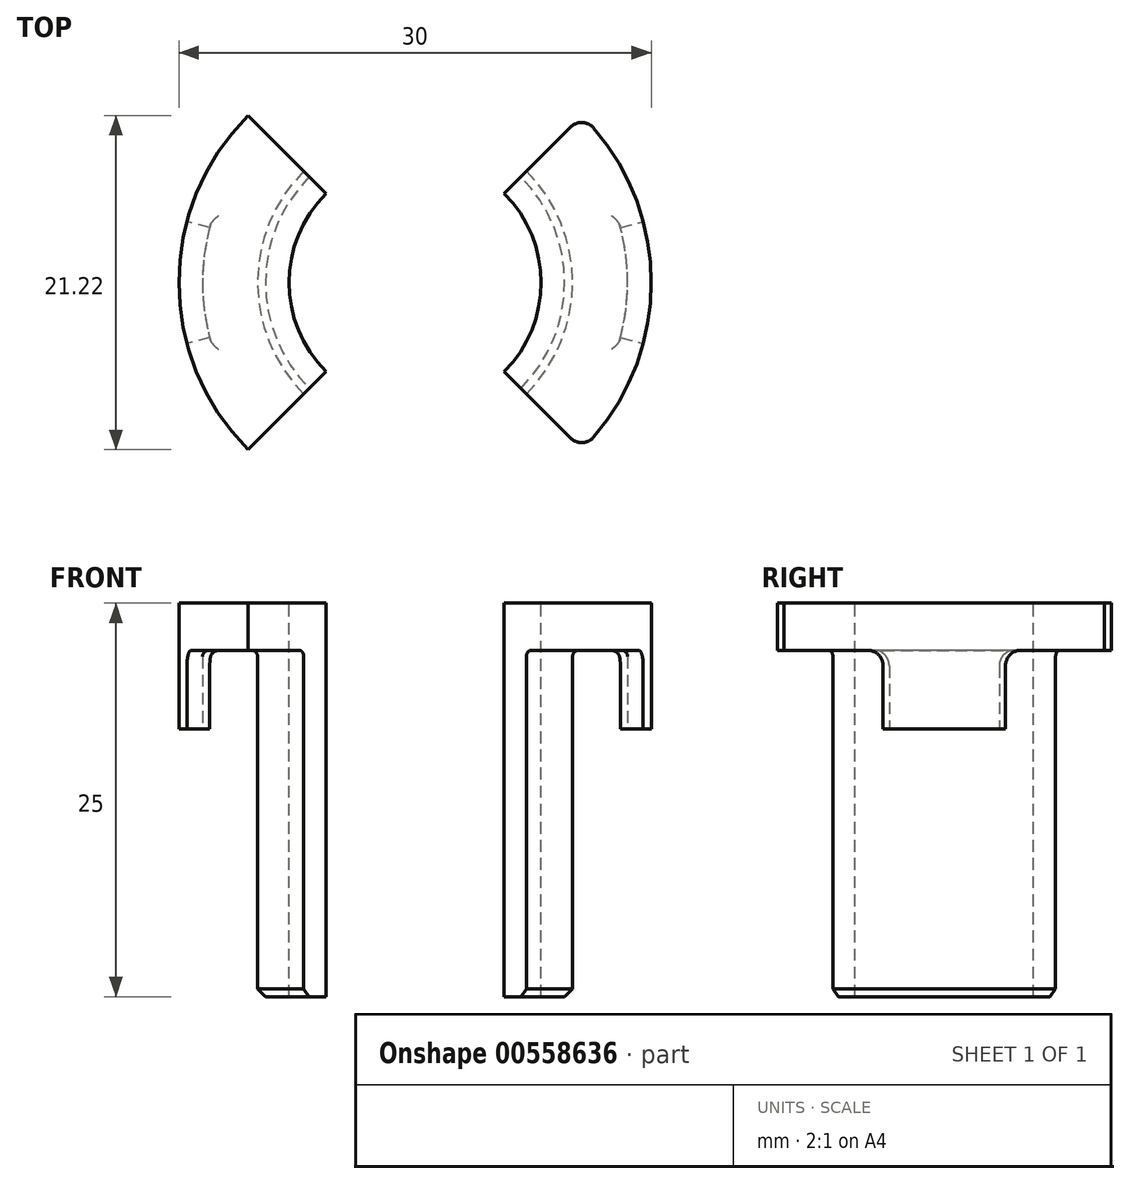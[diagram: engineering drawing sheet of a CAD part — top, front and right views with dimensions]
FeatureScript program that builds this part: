
annotation { "Feature Type Name" : "Feature", "Feature Type Description" : "" }
export const myFeature = defineFeature(function(context is Context, id is Id, definition is map)
    precondition{}
    {
        {
            var Q0;
            Q0=qCreatedBy(makeId("Top.planeOp"),FACE);
            var sketch = newSketch(context, id + "F0", { "sketchPlane" : qUnion([Q0])});
            skCircle(sketch, "E0", {"center": v(0, 0) * mm, "radius": 10 * mm});
            skCircle(sketch, "E1", {"center": v(0, 0) * mm, "radius": 8 * mm});
            skSolve(sketch);
        }
        {
            var Q0;
            Q0 = qSketchRegion(id + "F0", true);
            extrude(context, id + "F1", {"entities" : qUnion([Q0]), "oppositeDirection" : true, "depth" : 25 * mm, "offsetDistance" : 25 * mm});
        }
        {
            var Q0;
            Q0=qCreatedBy(makeId("Top.planeOp"),FACE);
            var sketch = newSketch(context, id + "F2", { "sketchPlane" : qUnion([Q0])});
            skCircle(sketch, "E2", {"center": v(0, 0) * mm, "radius": 15 * mm});
            skCircle(sketch, "E3.0", {"center": v(0, 0) * mm, "radius": 8 * mm});
            skSolve(sketch);
        }
        {
            var Q0;
            Q0 = qSketchRegion(id + "F2", true);
            extrude(context, id + "F3", {"entities" : qUnion([Q0]), "operationType" : NewBodyOperationType.ADD, "oppositeDirection" : true, "depth" : 8 * mm, "offsetDistance" : 25 * mm});
        }
        {
            var Q0;
            Q0=makeQuery(id+"F3.opExtrude","CAP_FACE",FACE,{"disambiguationData":[OSD([sQuery(id+"F2.wireOp",EDGE,"E2"),sQuery(id+"F2.wireOp",EDGE,"E3.0")])],"isStart":false});
            var sketch = newSketch(context, id + "F4", { "sketchPlane" : qUnion([Q0])});
            skCircle(sketch, "E4", {"center": v(0, 0) * mm, "radius": 13.5 * mm});
            skCircle(sketch, "E5.0", {"center": v(0, 0) * mm, "radius": 10 * mm});
            skSolve(sketch);
        }
        {
            var Q0;
            Q0 = qSketchRegion(id + "F4", true);
            extrude(context, id + "F5", {"entities" : qUnion([Q0]), "operationType" : NewBodyOperationType.REMOVE, "oppositeDirection" : true, "depth" : 5 * mm, "offsetDistance" : 25 * mm});
        }
        {
            var Q0;
            Q0=makeQuery(id+"F5.boolean.opBoolean","COPY",EDGE,{"derivedFrom":makeQuery(id+"F5.opExtrude","CAP_EDGE",EDGE,{"disambiguationData":[OSD([sQuery(id+"F4.wireOp",EDGE,"E4")])],"isStart":false})});
            var Q1;
            Q1=makeQuery(id+"F5.boolean.opBoolean","COPY",EDGE,{"derivedFrom":makeQuery(id+"F5.opExtrude","CAP_EDGE",EDGE,{"disambiguationData":[OSD([sQuery(id+"F4.wireOp",EDGE,"E5.0")])],"isStart":false})});
            fillet(context, id + "F6", {"entities" : qUnion([Q0, Q1]), "radius" : .4 * mm, "tangentPropagation" : true, "allowEdgeOverflow" : false});
        }
        {
            var Q0;
            Q0=qCreatedBy(makeId("Top.planeOp"),FACE);
            var sketch = newSketch(context, id + "F7", { "sketchPlane" : qUnion([Q0])});
            skLineSegment(sketch, "E6", {"start": v(0, 0) * mm, "end": v(20, 0) * mm, "construction": true});
            skLineSegment(sketch, "E7", {"start": v(0, 0) * mm, "end": v(0, 21.36) * mm, "construction": true});
            skArc(sketch, "E8.0", {"start": v(5.66, 5.66) * mm, "mid": v(0, 8) * mm, "end": v(-5.66, 5.66) * mm});
            skLineSegment(sketch, "E9", {"start": v(0, 0) * mm, "end": v(14.8, 14.8) * mm, "construction": true});
            skArc(sketch, "E10.0", {"start": v(10.6, 10.6) * mm, "mid": v(0, 15) * mm, "end": v(-10.6, 10.6) * mm});
            skLineSegment(sketch, "E11", {"start": v(5.66, 5.66) * mm, "end": v(10.6, 10.6) * mm});
            skLineSegment(sketch, "E12.MirrorCS", {"start": v(-5.66, 5.66) * mm, "end": v(-10.6, 10.6) * mm});
            skArc(sketch, "E13.MirrorCS", {"start": v(5.66, -5.66) * mm, "mid": v(0, -8) * mm, "end": v(-5.66, -5.66) * mm});
            skArc(sketch, "E14.MirrorCS", {"start": v(10.6, -10.6) * mm, "mid": v(0, -15) * mm, "end": v(-10.6, -10.6) * mm});
            skLineSegment(sketch, "E15.MirrorCS", {"start": v(-5.66, -5.66) * mm, "end": v(-10.6, -10.6) * mm});
            skLineSegment(sketch, "E16.MirrorCS", {"start": v(5.66, -5.66) * mm, "end": v(10.6, -10.6) * mm});
            skSolve(sketch);
        }
        {
            var Q0;
            Q0 = qSketchRegion(id + "F7", true);
            extrude(context, id + "F8", {"entities" : qUnion([Q0]), "operationType" : NewBodyOperationType.REMOVE, "oppositeDirection" : true, "depth" : 25 * mm, "offsetDistance" : 25 * mm});
        }
        {
            var Q0;
            {var subQ0=sQuery(id+"F2.wireOp",EDGE,"E2");Q0=makeQuery(id+"F8.boolean.opBoolean","SPLIT",FACE,{"disambiguationData":[TD([makeQuery(id+"F8.opExtrude","SWEPT_FACE",FACE,{"disambiguationData":[OSD([sQuery(id+"F7.wireOp",EDGE,"E11")])]})])],"derivedFrom":makeQuery(id+"F3.opExtrude","CAP_FACE",FACE,{"disambiguationData":[OSD([subQ0,sQuery(id+"F2.wireOp",EDGE,"E3.0")])],"isStart":false})});}
            var sketch = newSketch(context, id + "F9", { "sketchPlane" : qUnion([Q0])});
            skLineSegment(sketch, "E17", {"start": v(0, 0) * mm, "end": v(21.72, 0) * mm, "construction": true});
            skLineSegment(sketch, "E18", {"start": v(0, 0) * mm, "end": v(0, 13.45) * mm, "construction": true});
            skLineSegment(sketch, "E19", {"start": v(0, 0) * mm, "end": v(16.68, 4.47) * mm, "construction": true});
            skLineSegment(sketch, "E20", {"start": v(10.63, 2.85) * mm, "end": v(15.45, 4.14) * mm});
            skArc(sketch, "E21", {"start": v(10.63, 2.85) * mm, "mid": v(0, 11) * mm, "end": v(-10.63, 2.85) * mm});
            skArc(sketch, "E22", {"start": v(15.45, 4.14) * mm, "mid": v(0, 16) * mm, "end": v(-15.45, 4.14) * mm});
            skLineSegment(sketch, "E23.MirrorCS", {"start": v(-10.63, 2.85) * mm, "end": v(-15.45, 4.14) * mm});
            skLineSegment(sketch, "E24.MirrorCS", {"start": v(10.63, -2.85) * mm, "end": v(15.45, -4.14) * mm});
            skLineSegment(sketch, "E25.MirrorCS", {"start": v(-10.63, -2.85) * mm, "end": v(-15.45, -4.14) * mm});
            skArc(sketch, "E26.MirrorCS", {"start": v(10.63, -2.85) * mm, "mid": v(0, -11) * mm, "end": v(-10.63, -2.85) * mm});
            skArc(sketch, "E27.MirrorCS", {"start": v(15.45, -4.14) * mm, "mid": v(0, -16) * mm, "end": v(-15.45, -4.14) * mm});
            skSolve(sketch);
        }
        {
            var Q0;
            Q0 = qSketchRegion(id + "F9", true);
            var Q1;
            {var subQ0=sQuery(id+"F4.wireOp",EDGE,"E4");var subQ1=sQuery(id+"F4.wireOp",EDGE,"E5.0");Q1=makeQuery(id+"F8.boolean.opBoolean","SPLIT",FACE,{"disambiguationData":[TD([makeQuery(id+"F8.opExtrude","SWEPT_FACE",FACE,{"disambiguationData":[OSD([sQuery(id+"F7.wireOp",EDGE,"E11")])]})])],"derivedFrom":makeQuery(id+"F5.boolean.opBoolean","COPY",FACE,{"derivedFrom":makeQuery(id+"F5.opExtrude","CAP_FACE",FACE,{"disambiguationData":[OSD([subQ0,subQ1])],"isStart":false})})});}
            extrude(context, id + "F10", {"entities" : qUnion([Q0]), "operationType" : NewBodyOperationType.REMOVE, "endBound" : BoundingType.UP_TO_SURFACE, "oppositeDirection" : true, "depth" : 25 * mm, "endBoundEntityFace" : qUnion([Q1]), "offsetDistance" : 25 * mm});
        }
        {
            var Q0;
            Q0=makeQuery(id+"F10.boolean.opBoolean","COPY",EDGE,{"derivedFrom":makeQuery(id+"F10.opExtrude","CAP_EDGE",EDGE,{"disambiguationData":[OSD([sQuery(id+"F9.wireOp",EDGE,"E25.MirrorCS")])],"isStart":false})});
            var Q1;
            Q1=makeQuery(id+"F10.boolean.opBoolean","COPY",EDGE,{"derivedFrom":makeQuery(id+"F10.opExtrude","CAP_EDGE",EDGE,{"disambiguationData":[OSD([sQuery(id+"F9.wireOp",EDGE,"E23.MirrorCS")])],"isStart":false})});
            var Q2;
            Q2=makeQuery(id+"F10.boolean.opBoolean","COPY",EDGE,{"derivedFrom":makeQuery(id+"F10.opExtrude","CAP_EDGE",EDGE,{"disambiguationData":[OSD([sQuery(id+"F9.wireOp",EDGE,"E24.MirrorCS")])],"isStart":false})});
            var Q3;
            Q3=makeQuery(id+"F10.boolean.opBoolean","COPY",EDGE,{"derivedFrom":makeQuery(id+"F10.opExtrude","CAP_EDGE",EDGE,{"disambiguationData":[OSD([sQuery(id+"F9.wireOp",EDGE,"E20")])],"isStart":false})});
            fillet(context, id + "F11", {"entities" : qUnion([Q0, Q1, Q2, Q3]), "radius" : 1 * mm, "tangentPropagation" : true, "allowEdgeOverflow" : false});
        }
        {
            var Q0;
            Q0=makeQuery(id+"F8.boolean.opBoolean","COPY",EDGE,{"derivedFrom":makeQuery(id+"F8.opExtrude","SWEPT_EDGE",EDGE,{"disambiguationData":[OSD([sQuery(id+"F7.wireOp",EDGE,"E14.MirrorCS"),sQuery(id+"F7.wireOp",EDGE,"E16.MirrorCS")])]})});
            var Q1;
            Q1=makeQuery(id+"F8.boolean.opBoolean","COPY",EDGE,{"derivedFrom":makeQuery(id+"F8.opExtrude","SWEPT_EDGE",EDGE,{"disambiguationData":[OSD([sQuery(id+"F7.wireOp",EDGE,"E10.0"),sQuery(id+"F7.wireOp",EDGE,"E11")])]})});
            var Q2;
            Q2=makeQuery(id+"F8.boolean.opBoolean","COPY",EDGE,{"derivedFrom":makeQuery(id+"F8.opExtrude","SWEPT_EDGE",EDGE,{"disambiguationData":[OSD([sQuery(id+"F7.wireOp",EDGE,"E10.0"),sQuery(id+"F7.wireOp",EDGE,"E12.MirrorCS")])]})});
            var Q3;
            Q3=makeQuery(id+"F8.boolean.opBoolean","COPY",EDGE,{"derivedFrom":makeQuery(id+"F8.opExtrude","SWEPT_EDGE",EDGE,{"disambiguationData":[OSD([sQuery(id+"F7.wireOp",EDGE,"E14.MirrorCS"),sQuery(id+"F7.wireOp",EDGE,"E15.MirrorCS")])]})});
            fillet(context, id + "F12", {"entities" : qUnion([Q0, Q1, Q2, Q3]), "radius" : 1 * mm, "tangentPropagation" : true, "allowEdgeOverflow" : false});
        }
        {
            var Q0;
            {var subQ0=sQuery(id+"F0.wireOp",EDGE,"E0");Q0=makeQuery(id+"F8.boolean.opBoolean","SPLIT",EDGE,{"disambiguationData":[TD([makeQuery(id+"F8.opExtrude","SWEPT_FACE",FACE,{"disambiguationData":[OSD([sQuery(id+"F7.wireOp",EDGE,"E12.MirrorCS")])]})])],"derivedFrom":makeQuery(id+"F1.opExtrude","CAP_EDGE",EDGE,{"disambiguationData":[OSD([subQ0])],"isStart":false})});}
            var Q1;
            {var subQ0=sQuery(id+"F0.wireOp",EDGE,"E0");Q1=makeQuery(id+"F8.boolean.opBoolean","SPLIT",EDGE,{"disambiguationData":[TD([makeQuery(id+"F8.opExtrude","SWEPT_FACE",FACE,{"disambiguationData":[OSD([sQuery(id+"F7.wireOp",EDGE,"E11")])]})])],"derivedFrom":makeQuery(id+"F1.opExtrude","CAP_EDGE",EDGE,{"disambiguationData":[OSD([subQ0])],"isStart":false})});}
            chamfer(context, id + "F13", {"entities" : qUnion([Q0, Q1]), "width" : .5 * mm, "tangentPropagation" : true});
        }
    });
